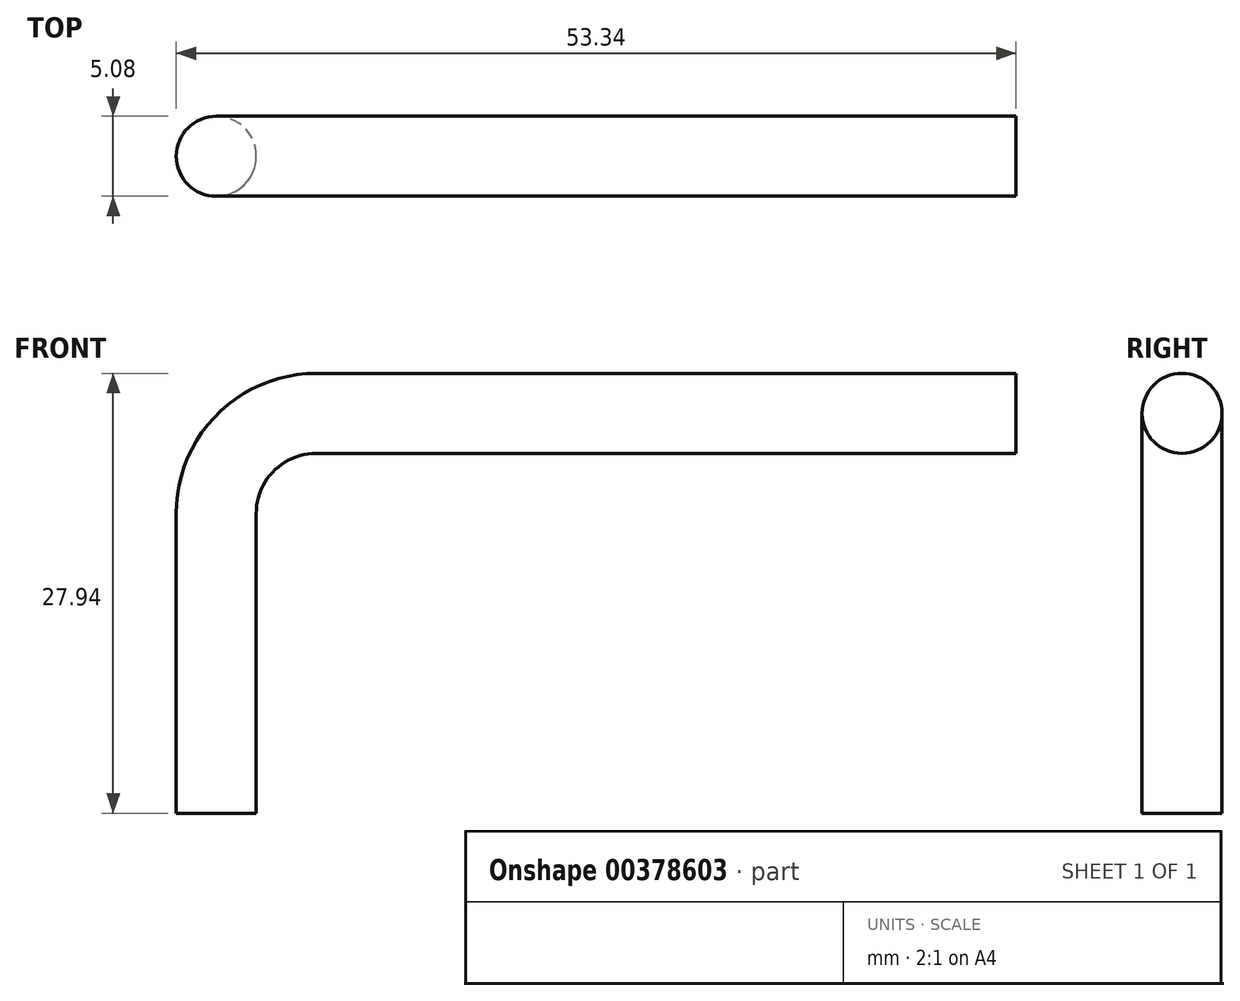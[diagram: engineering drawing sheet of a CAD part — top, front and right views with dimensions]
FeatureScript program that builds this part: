
annotation { "Feature Type Name" : "Feature", "Feature Type Description" : "" }
export const myFeature = defineFeature(function(context is Context, id is Id, definition is map)
    precondition{}
    {
        {
            var Q0;
            Q0=qCreatedBy(makeId("Front.planeOp"),FACE);
            var sketch = newSketch(context, id + "F0", { "sketchPlane" : qUnion([Q0])});
            skLineSegment(sketch, "E0", {"start": v(0, 0) * mm, "end": v(0, 19.05) * mm});
            skLineSegment(sketch, "E1", {"start": v(6.35, 25.4) * mm, "end": v(50.8, 25.4) * mm});
            skPoint(sketch, "E2.visualSharp", {"position": v(0, 25.4) * mm});
            skArc(sketch, "E2.filletArc", {"start": v(6.35, 25.4) * mm, "mid": v(1.86, 23.54) * mm, "end": v(0, 19.05) * mm});
            skSolve(sketch);
        }
        {
            var Q0;
            Q0=qCreatedBy(makeId("Top.planeOp"),FACE);
            var sketch = newSketch(context, id + "F1", { "sketchPlane" : qUnion([Q0])});
            skCircle(sketch, "E3", {"center": v(0, 0) * mm, "radius": 2.54 * mm});
            skSolve(sketch);
        }
        {
            var Q0;
            Q0=makeQuery(id+"F1.imprint","IMPRINT",FACE,{"disambiguationData":[TD([[makeQuery(id+"F1.imprint","IMPRINT",EDGE,{"derivedFrom":sQuery(id+"F1.wireOp",EDGE,"E3")}),1.0]])]});
            var Q1;
            Q1=sQuery(id+"F0.wireOp",EDGE,"E0");
            var Q2;
            Q2=sQuery(id+"F0.wireOp",EDGE,"E2.filletArc");
            var Q3;
            Q3=sQuery(id+"F0.wireOp",EDGE,"E1");
            sweep(context, id + "F2", {"profiles" : qUnion([Q0]), "path" : qUnion([Q1, Q2, Q3])});
        }
    });
